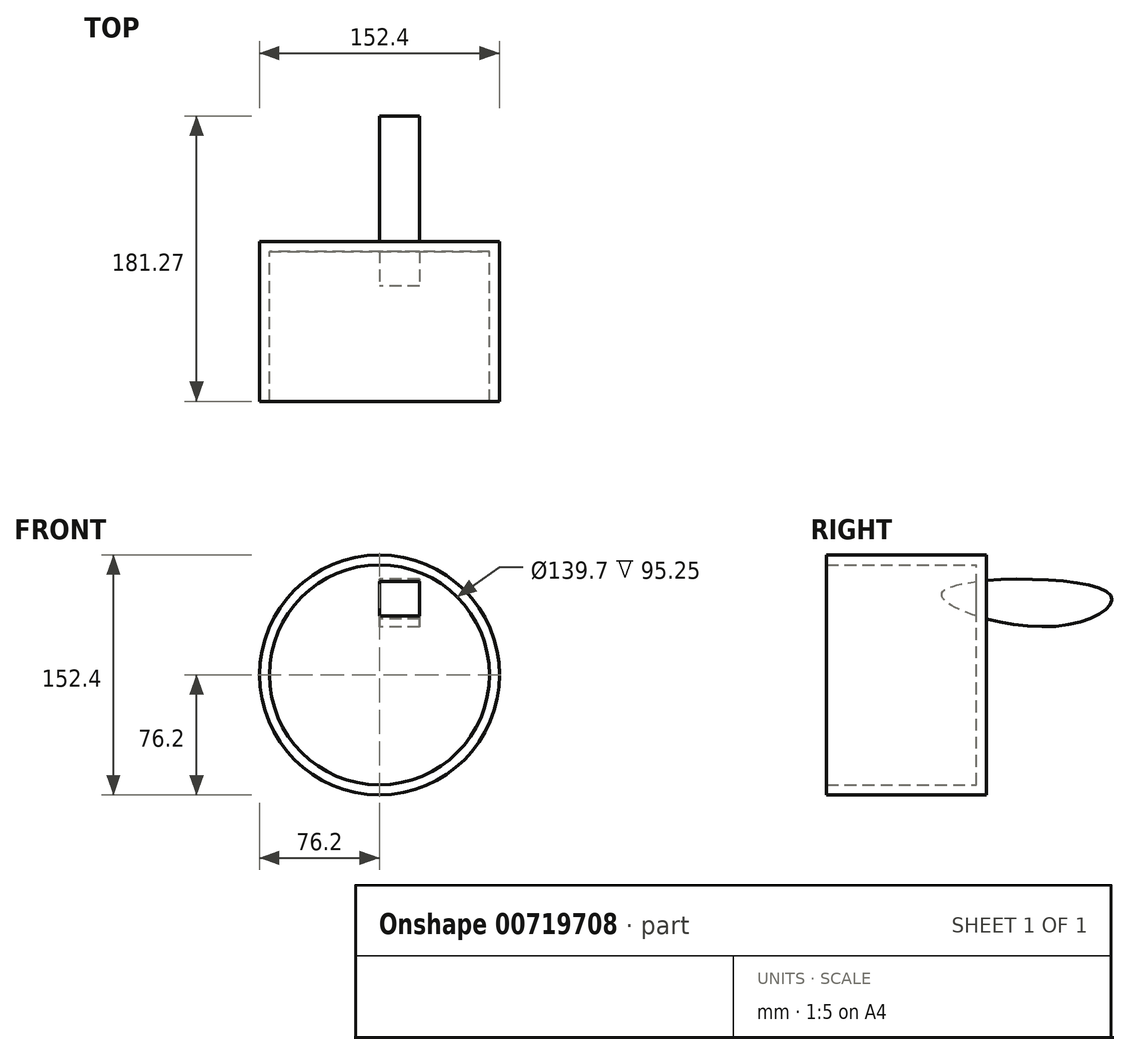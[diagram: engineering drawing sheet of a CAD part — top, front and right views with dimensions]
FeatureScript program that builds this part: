
annotation { "Feature Type Name" : "Feature", "Feature Type Description" : "" }
export const myFeature = defineFeature(function(context is Context, id is Id, definition is map)
    precondition{}
    {
        {
            var Q0;
            Q0=qCreatedBy(makeId("Front.planeOp"),FACE);
            var sketch = newSketch(context, id + "F0", { "sketchPlane" : qUnion([Q0])});
            skCircle(sketch, "E0", {"center": v(0, 0) * mm, "radius": 76.2 * mm});
            skCircle(sketch, "E1", {"center": v(0, 0) * mm, "radius": 69.85 * mm});
            skSolve(sketch);
        }
        {
            var Q0;
            Q0 = qSketchRegion(id + "F0", true);
            extrude(context, id + "F1", {"entities" : qUnion([Q0]), "depth" : 25.4 * mm, "offsetDistance" : 25.4 * mm});
        }
        {
            var Q0;
            Q0=makeQuery(id+"F1.opExtrude","CAP_FACE",FACE,{"disambiguationData":[OSD([sQuery(id+"F0.wireOp",EDGE,"E0"),sQuery(id+"F0.wireOp",EDGE,"E1")])],"isStart":false});
            extrude(context, id + "F2", {"entities" : qUnion([Q0]), "operationType" : NewBodyOperationType.ADD, "depth" : 76.2 * mm, "offsetDistance" : 25.4 * mm});
        }
        {
            var Q0;
            Q0=qCreatedBy(makeId("Front.planeOp"),FACE);
            var sketch = newSketch(context, id + "F3", { "sketchPlane" : qUnion([Q0])});
            skCircle(sketch, "E2", {"center": v(0, 0) * mm, "radius": 70.05 * mm});
            skSolve(sketch);
        }
        {
            var Q0;
            Q0 = qSketchRegion(id + "F3", true);
            extrude(context, id + "F4", {"entities" : qUnion([Q0]), "operationType" : NewBodyOperationType.ADD, "depth" : 6.35 * mm, "offsetDistance" : 25.4 * mm});
        }
        {
            var Q0;
            Q0=qCreatedBy(makeId("Right.planeOp"),FACE);
            var sketch = newSketch(context, id + "F5", { "sketchPlane" : qUnion([Q0])});
            skFitSpline(sketch, "E3", {"points": [v(-27.62, 52.8) * mm, v(77.5, 52.1) * mm, v(45.02, 30.98) * mm, v(-27.62, 52.8) * mm]});
            skSolve(sketch);
        }
        {
            var Q0;
            Q0 = qSketchRegion(id + "F5", true);
            extrude(context, id + "F6", {"entities" : qUnion([Q0]), "operationType" : NewBodyOperationType.ADD, "depth" : 25.4 * mm, "offsetDistance" : 25.4 * mm});
        }
    });
